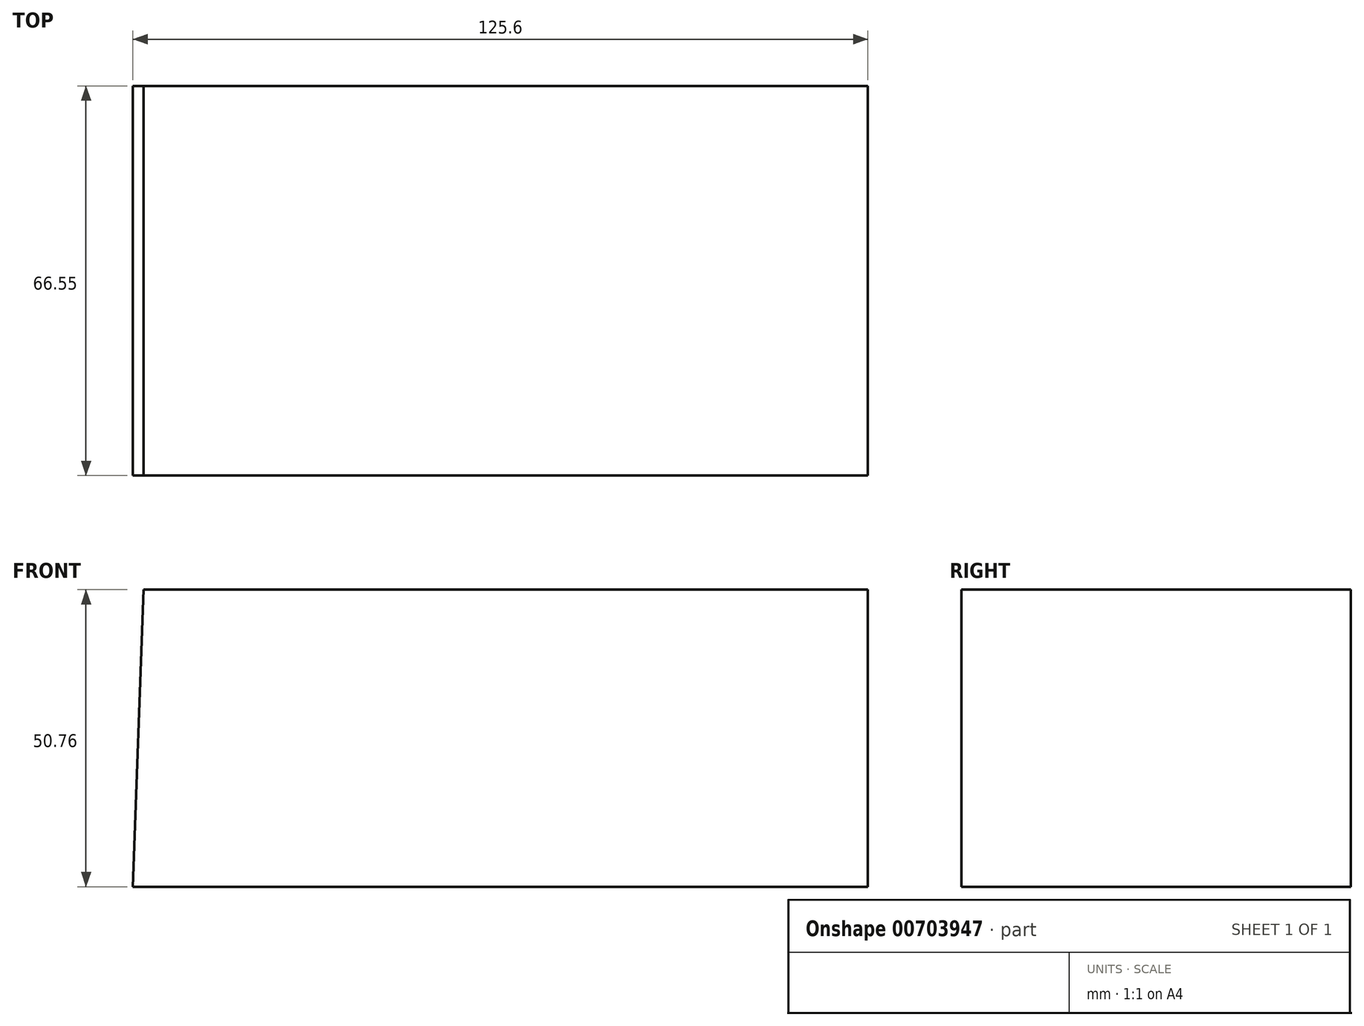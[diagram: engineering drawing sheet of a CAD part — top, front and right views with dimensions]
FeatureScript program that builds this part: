
annotation { "Feature Type Name" : "Feature", "Feature Type Description" : "" }
export const myFeature = defineFeature(function(context is Context, id is Id, definition is map)
    precondition{}
    {
        {
            var Q0;
            Q0=qCreatedBy(makeId("Front.planeOp"),FACE);
            var sketch = newSketch(context, id + "F0", { "sketchPlane" : qUnion([Q0])});
            skLineSegment(sketch, "E0", {"start": v(-64.43, 0) * mm, "end": v(61.17, 0) * mm});
            skLineSegment(sketch, "E1", {"start": v(61.17, 0) * mm, "end": v(61.17, 50.76) * mm});
            skLineSegment(sketch, "E2", {"start": v(61.17, 50.76) * mm, "end": v(-62.58, 50.76) * mm});
            skLineSegment(sketch, "E3", {"start": v(-62.58, 50.76) * mm, "end": v(-64.43, 0) * mm});
            skSolve(sketch);
        }
        {
            var Q0;
            Q0=makeQuery(id+"F0.imprint","IMPRINT",FACE,{"disambiguationData":[TD([[makeQuery(id+"F0.imprint","IMPRINT",EDGE,{"derivedFrom":sQuery(id+"F0.wireOp",EDGE,"E0")}),1.0]])]});
            extrude(context, id + "F1", {"entities" : qUnion([Q0]), "oppositeDirection" : true, "depth" : 66.55 * mm, "offsetDistance" : 25.4 * mm});
        }
    });
